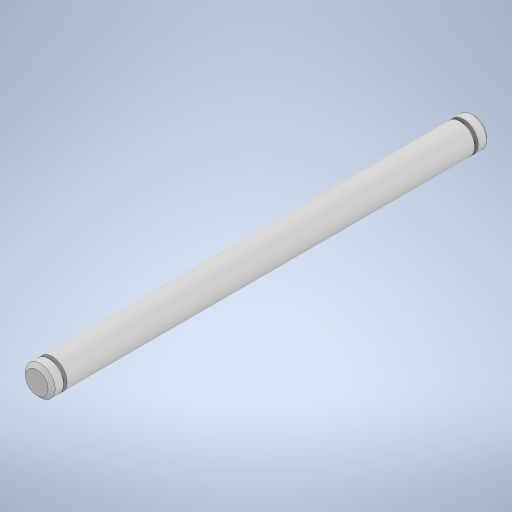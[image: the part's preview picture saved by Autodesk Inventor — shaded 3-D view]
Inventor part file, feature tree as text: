
AUTODESK INVENTOR PART (.ipt)
format: ipt  version: 2024 (Build 280153000, 153)  size: 264,192 bytes
history: native  units: in
note: dims shown in document units (in); Inventor stores cm internally (conversion verified against a paired STEP export)
features: extrude x3, sketch x3, chamfer x1, mirror x1, direct_edit x1, plane x1, other x1
ambient origin geometry x8: Origin, YZ Plane, XZ Plane, XY Plane, X Axis, Y Axis, Z Axis, Center Point
bodies: Solid1 (feature_tree)
feature tree (11):
  extrude  "Extrusion1"  Depth=1.7238in TaperAngle=0.0deg
  extrude  "Extrusion2"  Depth=0.015in TaperAngle=0.0deg
  extrude  "Extrusion3"  Depth=0.3937in TaperAngle=0.0deg
  chamfer  "Chamfer1"  Distance=0.015in Angle=45.0deg
  mirror  "Mirror1"
  direct_edit  "Direct Edit1"
  sketch  "Sketch1"  dims[d0=0.125in d1=1.7238in d2=0.0in]
  sketch  "Sketch2"  dims[d3=0.0938in d4=0.015in d5=0.0in]
  sketch  "Sketch3"  dims[d6=0.125in d7=0.05in d8=0.0in d9=0.015in d10=0.125in d11=45.0deg d12=3.937in d13=0.3937in d14=0.3937in]
  plane  "Work Plane1"
  other  "Scale1"
